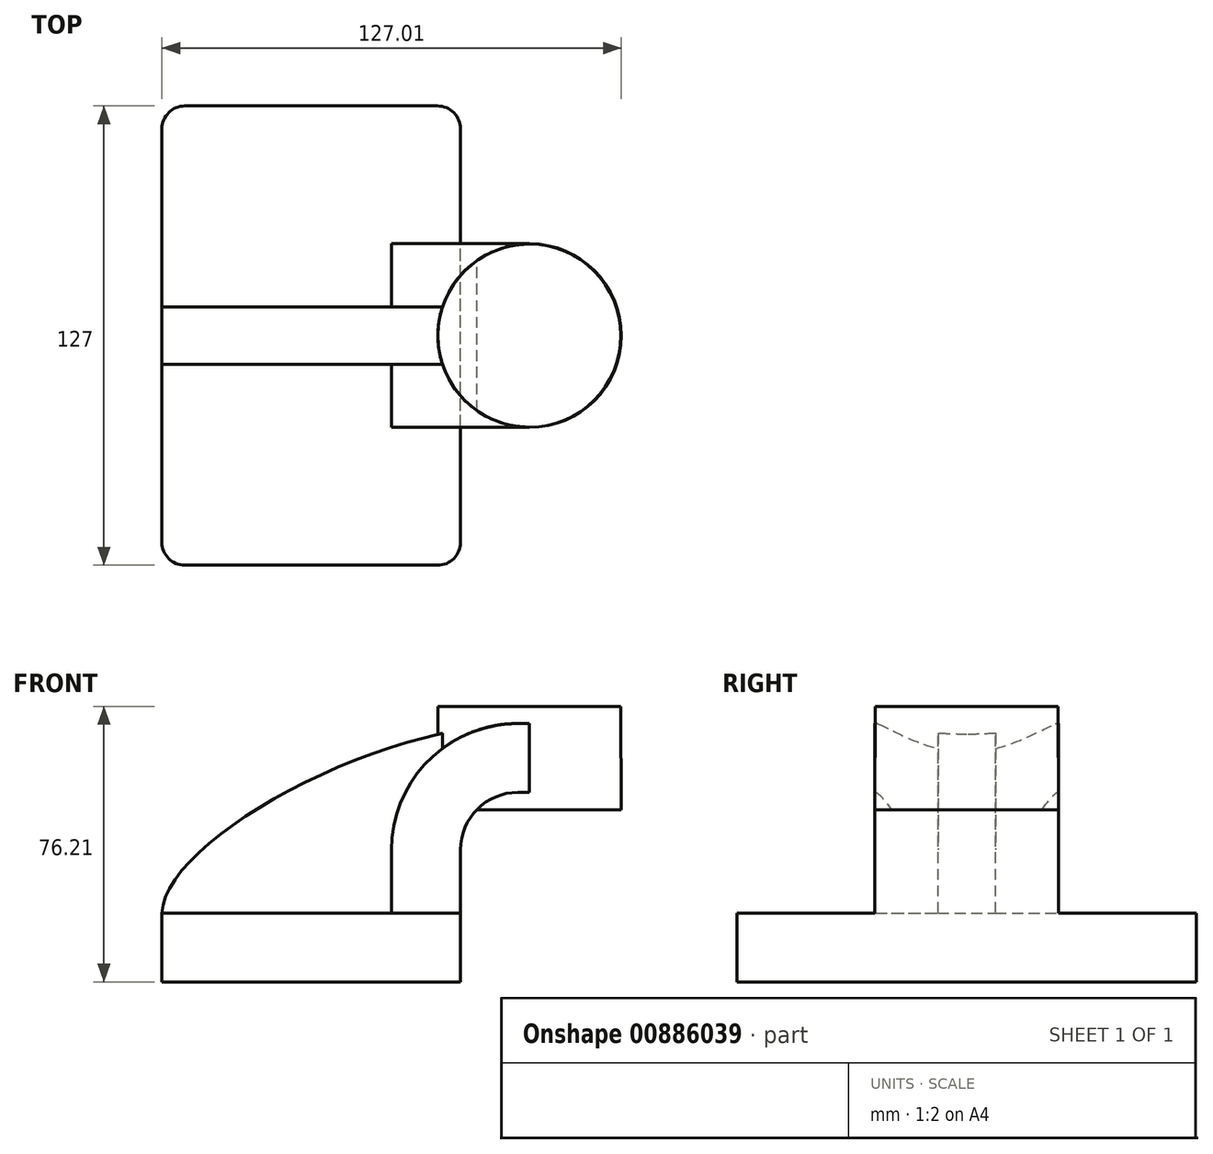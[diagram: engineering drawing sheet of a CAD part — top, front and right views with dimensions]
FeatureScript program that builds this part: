
annotation { "Feature Type Name" : "Feature", "Feature Type Description" : "" }
export const myFeature = defineFeature(function(context is Context, id is Id, definition is map)
    precondition{}
    {
        {
            var Q0;
            Q0=qCreatedBy(makeId("Front.planeOp"),FACE);
            var sketch = newSketch(context, id + "F0", { "sketchPlane" : qUnion([Q0])});
            skLineSegment(sketch, "E0.bottom", {"start": v(-41.28, 9.52) * mm, "end": v(41.27, 9.53) * mm});
            skLineSegment(sketch, "E0.top", {"start": v(-41.28, -9.53) * mm, "end": v(41.28, -9.53) * mm});
            skLineSegment(sketch, "E0.left", {"start": v(-41.28, 9.52) * mm, "end": v(-41.27, -9.53) * mm});
            skLineSegment(sketch, "E0.right", {"start": v(41.28, 9.53) * mm, "end": v(41.28, -9.52) * mm});
            skPoint(sketch, "E0.middle", {"position": v(0, 0) * mm});
            skLineSegment(sketch, "E1.bottom", {"start": v(111.12, 38.1) * mm, "end": v(60.33, 38.1) * mm});
            skLineSegment(sketch, "E1.top", {"start": v(111.12, 66.67) * mm, "end": v(60.33, 66.67) * mm});
            skLineSegment(sketch, "E1.left", {"start": v(111.12, 38.1) * mm, "end": v(111.12, 66.68) * mm});
            skLineSegment(sketch, "E1.right", {"start": v(60.33, 38.1) * mm, "end": v(60.33, 66.68) * mm});
            skPoint(sketch, "E1.middle", {"position": v(85.72, 52.39) * mm});
            skLineSegment(sketch, "E2", {"start": v(41.27, 9.53) * mm, "end": v(41.27, 27) * mm});
            skArc(sketch, "E3", {"start": v(41.27, 27) * mm, "mid": v(45.92, 38.23) * mm, "end": v(57.15, 42.88) * mm});
            skLineSegment(sketch, "E4", {"start": v(57.15, 42.88) * mm, "end": v(85.62, 42.88) * mm});
            skLineSegment(sketch, "E5.0", {"start": v(57.15, 61.93) * mm, "end": v(85.62, 61.93) * mm});
            skArc(sketch, "E5.1", {"start": v(22.22, 27) * mm, "mid": v(32.45, 51.7) * mm, "end": v(57.15, 61.93) * mm});
            skLineSegment(sketch, "E5.2", {"start": v(22.22, 9.53) * mm, "end": v(22.22, 27) * mm});
            skLineSegment(sketch, "E6", {"start": v(85.73, 38.1) * mm, "end": v(85.62, 66.67) * mm});
            skFitSpline(sketch, "E7", {"points": [v(-41.28, 9.53) * mm, v(57.15, 61.93) * mm], "startDerivative": vector(1.92, 59.23) * mm, "endDerivative": vector(123.91, 3.28) * mm});
            skSolve(sketch);
        }
        {
            var Q0;
            Q0=makeQuery(id+"F0.imprint","IMPRINT",FACE,{"disambiguationData":[TD([[makeQuery(id+"F0.imprint","IMPRINT",EDGE,{"derivedFrom":sQuery(id+"F0.wireOp",EDGE,"E0.top")}),1.0]])]});
            extrude(context, id + "F1", {"entities" : qUnion([Q0]), "endBound" : BoundingType.SYMMETRIC, "depth" : 127 * mm, "offsetDistance" : 25.4 * mm});
        }
        {
            var Q0;
            {var subQ1=sQuery(id+"F0.wireOp",EDGE,"E2");Q0=makeQuery(id+"F0.imprint","IMPRINT",FACE,{"disambiguationData":[TD([[makeQuery(id+"F0.imprint","IMPRINT",EDGE,{"derivedFrom":subQ1}),1.0]])]});}
            extrude(context, id + "F2", {"entities" : qUnion([Q0]), "operationType" : NewBodyOperationType.ADD, "endBound" : BoundingType.SYMMETRIC, "depth" : 50.8 * mm, "offsetDistance" : 25.4 * mm});
        }
        {
            var Q0;
            {var subQ3=sQuery(id+"F0.wireOp",EDGE,"E5.2");Q0=makeQuery(id+"F0.imprint","IMPRINT",FACE,{"disambiguationData":[TD([[makeQuery(id+"F0.imprint","IMPRINT",EDGE,{"derivedFrom":subQ3}),1.0]])]});}
            extrude(context, id + "F3", {"entities" : qUnion([Q0]), "operationType" : NewBodyOperationType.ADD, "endBound" : BoundingType.SYMMETRIC, "depth" : 15.88 * mm, "offsetDistance" : 25.4 * mm});
        }
        {
            var Q0;
            {var subQ6=sQuery(id+"F0.wireOp",EDGE,"E6");Q0=makeQuery(id+"F0.imprint","IMPRINT",FACE,{"disambiguationData":[TD([[makeQuery(id+"F0.imprint","IMPRINT",EDGE,{"derivedFrom":subQ6}),1.0]])]});}
            var Q1;
            Q1=sQuery(id+"F0.wireOp",EDGE,"E1.right");
            revolve(context, id + "F4", {"operationType" : NewBodyOperationType.ADD, "surfaceOperationType" : NewSurfaceOperationType.NEW, "entities" : qUnion([Q0]), "axis" : qUnion([Q1]), "revolveType" : RevolveType.FULL});
        }
        {
            var Q0;
            Q0=makeQuery(id+"F1.opExtrude","CAP_EDGE",EDGE,{"disambiguationData":[OSD([sQuery(id+"F0.wireOp",EDGE,"E0.right")])],"isStart":false});
            var Q1;
            Q1=makeQuery(id+"F1.opExtrude","CAP_EDGE",EDGE,{"disambiguationData":[OSD([sQuery(id+"F0.wireOp",EDGE,"E0.left")])],"isStart":false});
            var Q2;
            Q2=makeQuery(id+"F1.opExtrude","CAP_EDGE",EDGE,{"disambiguationData":[OSD([sQuery(id+"F0.wireOp",EDGE,"E0.right")])],"isStart":true});
            var Q3;
            Q3=makeQuery(id+"F1.opExtrude","CAP_EDGE",EDGE,{"disambiguationData":[OSD([sQuery(id+"F0.wireOp",EDGE,"E0.left")])],"isStart":true});
            fillet(context, id + "F5", {"entities" : qUnion([Q0, Q1, Q2, Q3]), "radius" : 6.35 * mm, "tangentPropagation" : true, "allowEdgeOverflow" : false});
        }
    });
